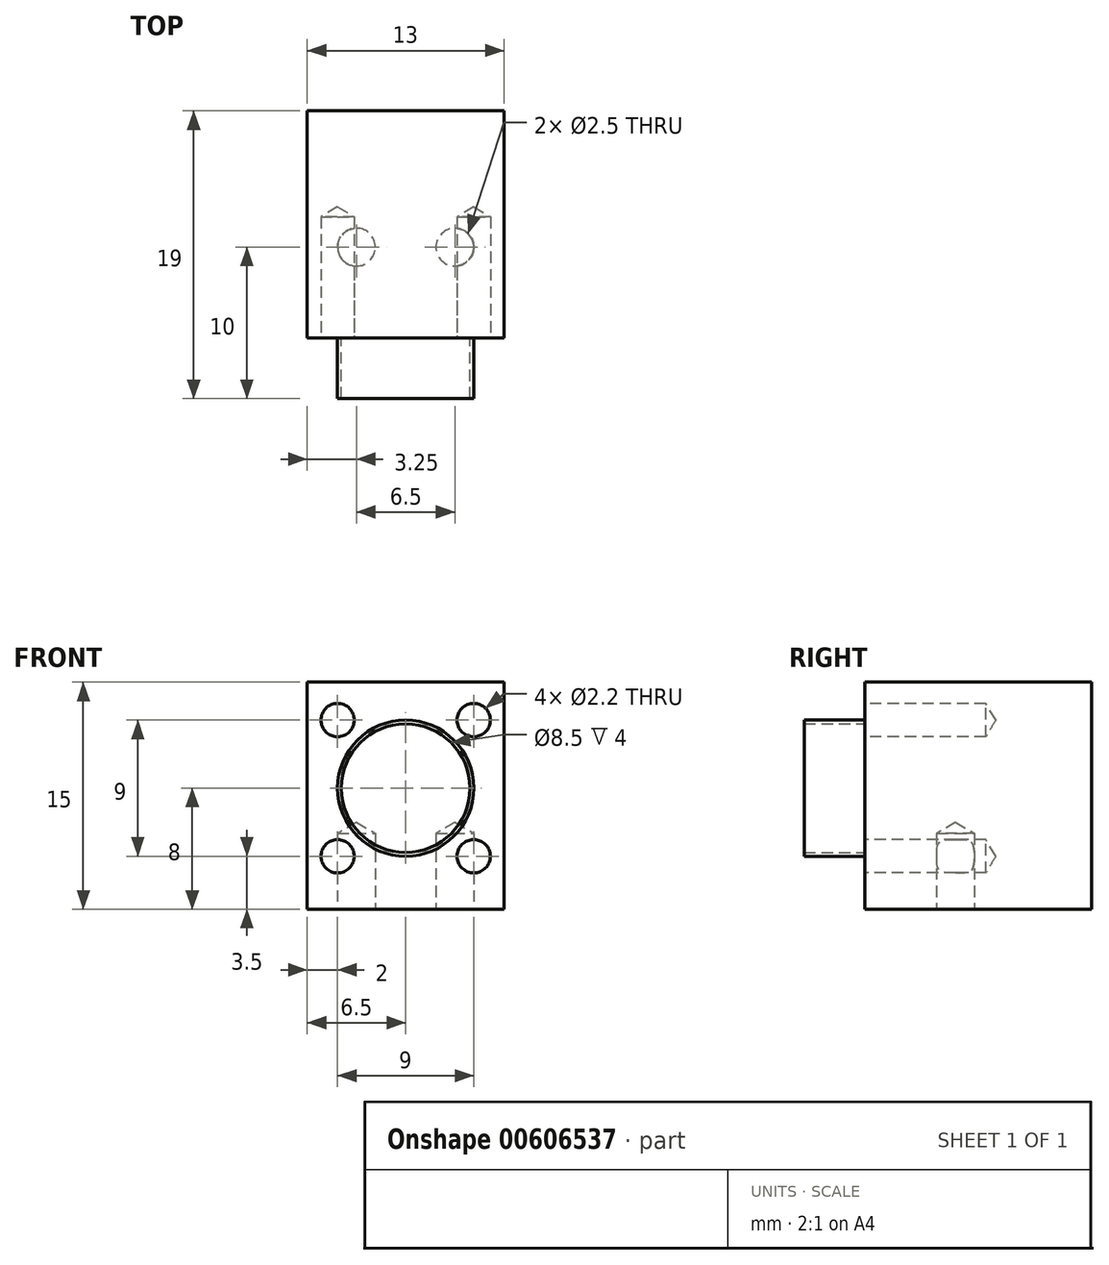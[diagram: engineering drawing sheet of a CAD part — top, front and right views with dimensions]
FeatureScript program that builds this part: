
annotation { "Feature Type Name" : "Feature", "Feature Type Description" : "" }
export const myFeature = defineFeature(function(context is Context, id is Id, definition is map)
    precondition{}
    {
        {
            var Q0;
            Q0=qCreatedBy(makeId("Front.planeOp"),FACE);
            var sketch = newSketch(context, id + "F0", { "sketchPlane" : qUnion([Q0])});
            skLineSegment(sketch, "E0.bottom", {"start": v(6.5, 7.5) * mm, "end": v(-6.5, 7.5) * mm});
            skLineSegment(sketch, "E0.top", {"start": v(6.5, -7.5) * mm, "end": v(-6.5, -7.5) * mm});
            skLineSegment(sketch, "E0.left", {"start": v(6.5, 7.5) * mm, "end": v(6.5, -7.5) * mm});
            skLineSegment(sketch, "E0.right", {"start": v(-6.5, 7.5) * mm, "end": v(-6.5, -7.5) * mm});
            skPoint(sketch, "E0.middle", {"position": v(0, 0) * mm});
            skPoint(sketch, "E1", {"position": v(-4.5, 5) * mm});
            skPoint(sketch, "E2", {"position": v(4.5, 5) * mm});
            skPoint(sketch, "E3", {"position": v(4.5, -4) * mm});
            skPoint(sketch, "E4", {"position": v(-4.5, -4) * mm});
            skCircle(sketch, "E5", {"center": v(0, 0.5) * mm, "radius": 4.5 * mm});
            skSolve(sketch);
        }
        {
            var Q0;
            Q0=makeQuery(id+"F0.imprint","IMPRINT",FACE,{"disambiguationData":[TD([[makeQuery(id+"F0.imprint","IMPRINT",EDGE,{"derivedFrom":sQuery(id+"F0.wireOp",EDGE,"E5")}),1.0]])]});
            extrude(context, id + "F1", {"entities" : qUnion([Q0]), "depth" : 4 * mm, "hasSecondDirection" : true, "secondDirectionOppositeDirection" : true, "secondDirectionDepth" : 15 * mm});
        }
        {
            var Q0;
            Q0=qSketchRegion(id+"F0",true);
            extrude(context, id + "F2", {"entities" : qUnion([Q0]), "operationType" : NewBodyOperationType.ADD, "oppositeDirection" : true, "depth" : 15 * mm});
        }
        {
            var Q0;
            Q0=sQuery(id+"F0.wireOp",VERTEX,"E2");
            var Q1;
            Q1=sQuery(id+"F0.wireOp",VERTEX,"E3");
            var Q2;
            Q2=sQuery(id+"F0.wireOp",VERTEX,"E1");
            var Q3;
            Q3=sQuery(id+"F0.wireOp",VERTEX,"E4");
            var Q4;
            Q4=makeQuery(id+"F1.opExtrude","SWEPT_BODY",BODY,{"disambiguationData":[OSD([sQuery(id+"F0.wireOp",EDGE,"E5")])]});
            hole(context, id + "F3", {"style" : HoleStyle.SIMPLE, "endStyle" : HoleEndStyle.BLIND, "holeDiameter" : 2.2 * mm, "holeDepth" : 8 * mm, "isTappedThrough" : true, "tappedDepth" : 12 * mm, "tapClearance" : 3, "locations" : qUnion([Q0, Q1, Q2, Q3]), "scope" : qUnion([Q4])});
        }
        {
            var Q0;
            Q0=sQuery(id+"F0.wireOp",VERTEX,"E5.center");
            var Q1;
            Q1=makeQuery(id+"F1.opExtrude","SWEPT_BODY",BODY,{"disambiguationData":[OSD([sQuery(id+"F0.wireOp",EDGE,"E5")])]});
            hole(context, id + "F4", {"style" : HoleStyle.SIMPLE, "endStyle" : HoleEndStyle.BLIND, "oppositeDirection" : true, "holeDiameter" : 8.5 * mm, "holeDepth" : 8 * mm, "isTappedThrough" : true, "tappedDepth" : 12 * mm, "tapClearance" : 3, "locations" : qUnion([Q0]), "scope" : qUnion([Q1])});
        }
        {
            var Q0;
            Q0=makeQuery(id+"F2.opExtrude","SWEPT_FACE",FACE,{"disambiguationData":[OSD([sQuery(id+"F0.wireOp",EDGE,"E0.top")])]});
            var sketch = newSketch(context, id + "F5", { "sketchPlane" : qUnion([Q0])});
            skPoint(sketch, "E6", {"position": v(-3.25, -6) * mm});
            skPoint(sketch, "E7", {"position": v(3.25, -6) * mm});
            skSolve(sketch);
        }
        {
            var Q0;
            Q0=sQuery(id+"F5.wireOp",VERTEX,"E6");
            var Q1;
            Q1=sQuery(id+"F5.wireOp",VERTEX,"E7");
            var Q2;
            Q2=makeQuery(id+"F1.opExtrude","SWEPT_BODY",BODY,{"disambiguationData":[OSD([sQuery(id+"F0.wireOp",EDGE,"E5")])]});
            hole(context, id + "F6", {"style" : HoleStyle.SIMPLE, "endStyle" : HoleEndStyle.BLIND, "standardTappedOrClearance" : lookupTablePath({ "standard" : "ISO", "engagement" : "75%", "pitch" : "0.5 mm", "size" : "M3", "type" : "Tapped" }), "standardBlindInLast" : lookupTablePath({ "standard" : "ISO", "engagement" : "75%", "pitch" : "0.5 mm", "size" : "M3", "type" : "Tapped" }), "holeDiameter" : 2.5 * mm, "showTappedDepth" : true, "holeDepth" : 5 * mm, "isTappedThrough" : true, "tappedDepth" : 3.5 * mm, "tapClearance" : 3, "locations" : qUnion([Q0, Q1]), "scope" : qUnion([Q2]), "majorDiameter" : 3 * mm});
        }
    });
